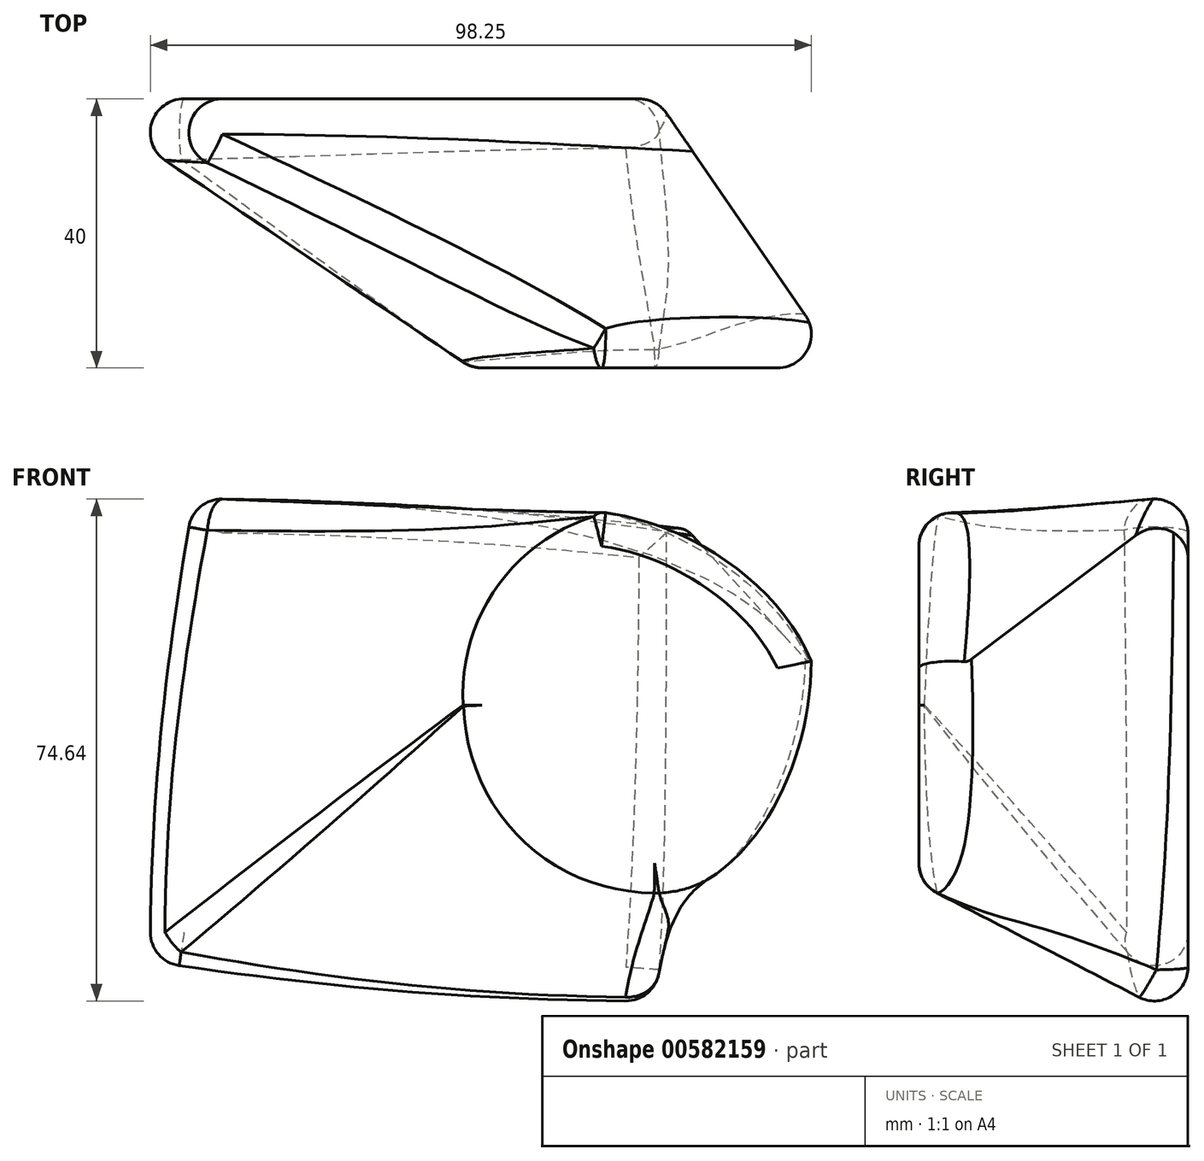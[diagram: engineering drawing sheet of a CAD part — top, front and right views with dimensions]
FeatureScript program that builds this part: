
annotation { "Feature Type Name" : "Feature", "Feature Type Description" : "" }
export const myFeature = defineFeature(function(context is Context, id is Id, definition is map)
    precondition{}
    {
        {
            var Q0;
            Q0=qCreatedBy(makeId("Front.planeOp"),FACE);
            cPlane(context, id + "F0", {"entities" : qUnion([Q0]), "cplaneType" : CPlaneType.OFFSET, "offset" : 40 * mm, "width" : 150 * mm, "height" : 150 * mm});
        }
        {
            var Q0;
            Q0=qCreatedBy(id+"F0.planeOp",FACE);
            var sketch = newSketch(context, id + "F1", { "sketchPlane" : qUnion([Q0])});
            skCircle(sketch, "E0", {"center": v(0, 0) * mm, "radius": 27.5 * mm});
            skSolve(sketch);
        }
        {
            var Q0;
            Q0=qCreatedBy(makeId("Front.planeOp"),FACE);
            var sketch = newSketch(context, id + "F2", { "sketchPlane" : qUnion([Q0])});
            skLineSegment(sketch, "E1.bottom", {"start": v(0, -48.17) * mm, "end": v(-86.57, -48.17) * mm});
            skLineSegment(sketch, "E1.top", {"start": v(0, 30.11) * mm, "end": v(-86.57, 30.11) * mm});
            skLineSegment(sketch, "E1.left", {"start": v(0, -48.17) * mm, "end": v(0, 30.11) * mm});
            skLineSegment(sketch, "E1.right", {"start": v(-86.57, -48.17) * mm, "end": v(-86.57, 30.11) * mm});
            skSolve(sketch);
        }
        {
            var Q0;
            Q0=makeQuery(id+"F2.imprint","IMPRINT",FACE,{"disambiguationData":[TD([[makeQuery(id+"F2.imprint","IMPRINT",EDGE,{"derivedFrom":sQuery(id+"F2.wireOp",EDGE,"E1.bottom")}),-1.0]])]});
            var Q1;
            Q1=makeQuery(id+"F1.imprint","IMPRINT",FACE,{"disambiguationData":[TD([[makeQuery(id+"F1.imprint","IMPRINT",EDGE,{"derivedFrom":sQuery(id+"F1.wireOp",EDGE,"E0")}),1.0]])]});
            loft(context, id + "F3", {"sheetProfilesArray" : [{ "sheetProfileEntities" : qUnion([Q0]) }, { "sheetProfileEntities" : qUnion([Q1]) }]});
        }
        {
            var Q0;
            Q0=makeQuery(id+"F3.opLoft","SWEPT_EDGE",EDGE,{"disambiguationData":[OSD([sQuery(id+"F1.wireOp",EDGE,"E0"),sQuery(id+"F2.wireOp",EDGE,"E1.bottom"),sQuery(id+"F2.wireOp",EDGE,"E1.top"),sQuery(id+"F2.wireOp",EDGE,"E1.right")])]});
            var Q1;
            Q1=makeQuery(id+"F3.opLoft","SWEPT_EDGE",EDGE,{"disambiguationData":[OSD([sQuery(id+"F1.wireOp",EDGE,"E0"),sQuery(id+"F2.wireOp",EDGE,"E1.top"),sQuery(id+"F2.wireOp",EDGE,"E1.left"),sQuery(id+"F2.wireOp",EDGE,"E1.right")])]});
            var Q2;
            Q2=makeQuery(id+"F3.opLoft","SWEPT_EDGE",EDGE,{"disambiguationData":[OSD([sQuery(id+"F2.wireOp",EDGE,"E1.bottom"),sQuery(id+"F2.wireOp",EDGE,"E1.left")])]});
            var Q3;
            Q3=makeQuery(id+"F3.opLoft","SWEPT_EDGE",EDGE,{"disambiguationData":[OSD([sQuery(id+"F1.wireOp",EDGE,"E0"),sQuery(id+"F2.wireOp",EDGE,"E1.bottom"),sQuery(id+"F2.wireOp",EDGE,"E1.top"),sQuery(id+"F2.wireOp",EDGE,"E1.left")])]});
            fillet(context, id + "F4", {"entities" : qUnion([Q0, Q1, Q2, Q3]), "radius" : 5 * mm, "tangentPropagation" : true, "allowEdgeOverflow" : false});
        }
        {
            var Q0;
            Q0=makeQuery(id+"F3.opLoft","MID_CAP_EDGE",EDGE,{"disambiguationData":[OSD([sQuery(id+"F1.wireOp",EDGE,"E0"),sQuery(id+"F2.wireOp",EDGE,"E1.bottom"),sQuery(id+"F2.wireOp",EDGE,"E1.top"),sQuery(id+"F2.wireOp",EDGE,"E1.left")])],"capPos":1.0});
            var Q1;
            Q1=makeQuery(id+"F3.opLoft","MID_CAP_EDGE",EDGE,{"disambiguationData":[OSD([sQuery(id+"F1.wireOp",EDGE,"E0"),sQuery(id+"F2.wireOp",EDGE,"E1.bottom"),sQuery(id+"F2.wireOp",EDGE,"E1.left")])],"capPos":1.0});
            var Q2;
            Q2=makeQuery(id+"F3.opLoft","MID_CAP_EDGE",EDGE,{"disambiguationData":[OSD([sQuery(id+"F1.wireOp",EDGE,"E0"),sQuery(id+"F2.wireOp",EDGE,"E1.bottom"),sQuery(id+"F2.wireOp",EDGE,"E1.top"),sQuery(id+"F2.wireOp",EDGE,"E1.left"),sQuery(id+"F2.wireOp",EDGE,"E1.right")])],"capPos":1.0});
            var Q3;
            Q3=makeQuery(id+"F3.opLoft","MID_CAP_EDGE",EDGE,{"disambiguationData":[OSD([sQuery(id+"F1.wireOp",EDGE,"E0"),sQuery(id+"F2.wireOp",EDGE,"E1.top"),sQuery(id+"F2.wireOp",EDGE,"E1.left"),sQuery(id+"F2.wireOp",EDGE,"E1.right")])],"capPos":1.0});
            var Q4;
            Q4=makeQuery(id+"F3.opLoft","MID_CAP_EDGE",EDGE,{"disambiguationData":[OSD([sQuery(id+"F2.wireOp",EDGE,"E1.bottom"),sQuery(id+"F2.wireOp",EDGE,"E1.top"),sQuery(id+"F2.wireOp",EDGE,"E1.left")])],"capPos":0.0});
            var Q5;
            {var subQ0=sQuery(id+"F2.wireOp",EDGE,"E1.bottom");var subQ1=sQuery(id+"F2.wireOp",EDGE,"E1.left");Q5=makeQuery(id+"F4.opFillet","BLEND_EDGE",EDGE,{"blendedFrom":[makeQuery(id+"F3.opLoft","SWEPT_EDGE",EDGE,{"disambiguationData":[OSD([subQ0,subQ1])]}),makeQuery(id+"F3.opLoft","CAP_FACE",FACE,{"disambiguationData":[OSD([makeQuery(id+"F2.imprint","IMPRINT",FACE,{"disambiguationData":[TD([[makeQuery(id+"F2.imprint","IMPRINT",EDGE,{"derivedFrom":subQ0}),-1.0]])]})])],"isStart":true})],"blendedInto":[makeQuery(id+"F3.opLoft","CAP_FACE",FACE,{"disambiguationData":[OSD([makeQuery(id+"F2.imprint","IMPRINT",FACE,{"disambiguationData":[TD([[makeQuery(id+"F2.imprint","IMPRINT",EDGE,{"derivedFrom":subQ0}),-1.0]])]})])],"isStart":true})]});}
            var Q6;
            Q6=makeQuery(id+"F3.opLoft","MID_CAP_EDGE",EDGE,{"disambiguationData":[OSD([sQuery(id+"F2.wireOp",EDGE,"E1.bottom"),sQuery(id+"F2.wireOp",EDGE,"E1.left"),sQuery(id+"F2.wireOp",EDGE,"E1.right")])],"capPos":0.0});
            var Q7;
            Q7=makeQuery(id+"F3.opLoft","MID_CAP_EDGE",EDGE,{"disambiguationData":[OSD([sQuery(id+"F2.wireOp",EDGE,"E1.bottom"),sQuery(id+"F2.wireOp",EDGE,"E1.top"),sQuery(id+"F2.wireOp",EDGE,"E1.right")])],"capPos":0.0});
            var Q8;
            Q8=makeQuery(id+"F3.opLoft","MID_CAP_EDGE",EDGE,{"disambiguationData":[OSD([sQuery(id+"F2.wireOp",EDGE,"E1.top"),sQuery(id+"F2.wireOp",EDGE,"E1.left"),sQuery(id+"F2.wireOp",EDGE,"E1.right")])],"capPos":0.0});
            var Q9;
            {var subQ0=sQuery(id+"F2.wireOp",EDGE,"E1.bottom");var subQ1=sQuery(id+"F2.wireOp",EDGE,"E1.top");var subQ2=sQuery(id+"F2.wireOp",EDGE,"E1.left");Q9=makeQuery(id+"F4.opFillet","BLEND_EDGE",EDGE,{"blendedFrom":[makeQuery(id+"F3.opLoft","SWEPT_EDGE",EDGE,{"disambiguationData":[OSD([sQuery(id+"F1.wireOp",EDGE,"E0"),subQ0,subQ1,subQ2])]}),makeQuery(id+"F3.opLoft","CAP_FACE",FACE,{"disambiguationData":[OSD([makeQuery(id+"F2.imprint","IMPRINT",FACE,{"disambiguationData":[TD([[makeQuery(id+"F2.imprint","IMPRINT",EDGE,{"derivedFrom":subQ0}),-1.0]])]})])],"isStart":true})],"blendedInto":[makeQuery(id+"F3.opLoft","CAP_FACE",FACE,{"disambiguationData":[OSD([makeQuery(id+"F2.imprint","IMPRINT",FACE,{"disambiguationData":[TD([[makeQuery(id+"F2.imprint","IMPRINT",EDGE,{"derivedFrom":subQ0}),-1.0]])]})])],"isStart":true})]});}
            fillet(context, id + "F5", {"entities" : qUnion([Q0, Q1, Q2, Q3, Q4, Q5, Q6, Q7, Q8, Q9]), "radius" : 5 * mm, "tangentPropagation" : true, "allowEdgeOverflow" : false});
        }
    });
